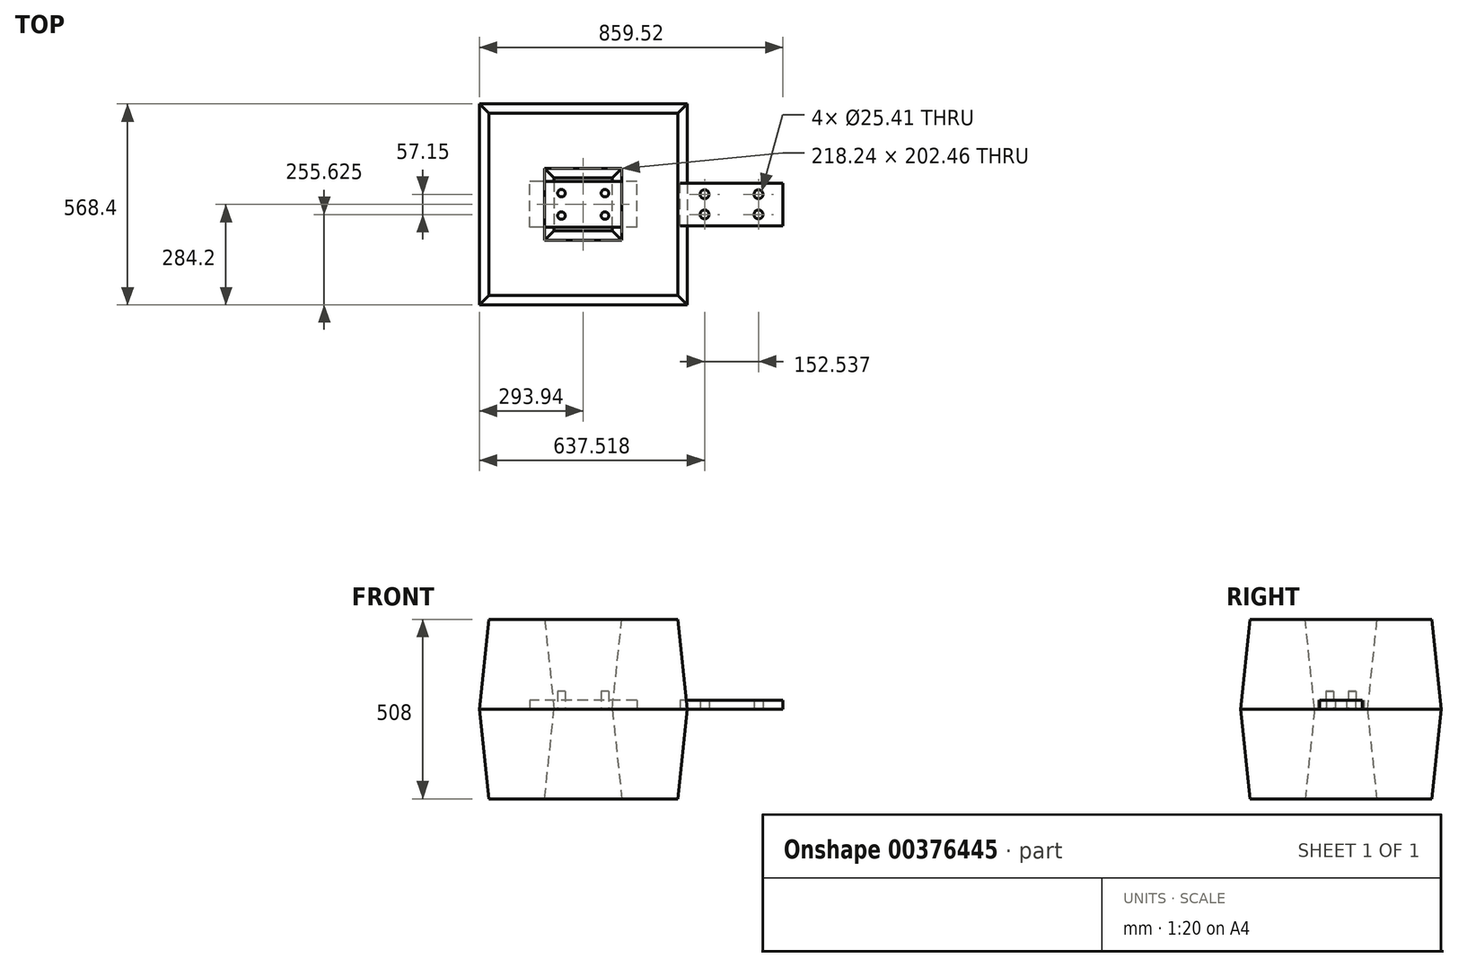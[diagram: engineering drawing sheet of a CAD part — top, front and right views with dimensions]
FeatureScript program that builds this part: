
annotation { "Feature Type Name" : "Feature", "Feature Type Description" : "" }
export const myFeature = defineFeature(function(context is Context, id is Id, definition is map)
    precondition{}
    {
        {
            var Q0;
            Q0=qCreatedBy(makeId("Top.planeOp"),FACE);
            var sketch = newSketch(context, id + "F0", { "sketchPlane" : qUnion([Q0])});
            skLineSegment(sketch, "E0.bottom", {"start": v(151.76, -65.22) * mm, "end": v(-151.76, -65.22) * mm});
            skLineSegment(sketch, "E0.top", {"start": v(151.76, 65.22) * mm, "end": v(-151.76, 65.22) * mm});
            skLineSegment(sketch, "E0.left", {"start": v(151.76, -65.22) * mm, "end": v(151.76, 65.22) * mm});
            skLineSegment(sketch, "E0.right", {"start": v(-151.76, -65.22) * mm, "end": v(-151.76, 65.22) * mm});
            skPoint(sketch, "E0.middle", {"position": v(0, 0) * mm});
            skSolve(sketch);
        }
        {
            var Q0;
            Q0 = qSketchRegion(id + "F0", true);
            extrude(context, id + "F1", {"entities" : qUnion([Q0]), "depth" : 25.4 * mm});
        }
        {
            var Q0;
            Q0=qCreatedBy(makeId("Top.planeOp"),FACE);
            var sketch = newSketch(context, id + "F2", { "sketchPlane" : qUnion([Q0])});
            skLineSegment(sketch, "E1.bottom", {"start": v(61.61, -31.77) * mm, "end": v(-61.61, -31.77) * mm, "construction": true});
            skLineSegment(sketch, "E1.top", {"start": v(61.61, 31.77) * mm, "end": v(-61.61, 31.77) * mm, "construction": true});
            skLineSegment(sketch, "E1.left", {"start": v(61.61, -31.77) * mm, "end": v(61.61, 31.77) * mm, "construction": true});
            skLineSegment(sketch, "E1.right", {"start": v(-61.61, -31.77) * mm, "end": v(-61.61, 31.77) * mm, "construction": true});
            skPoint(sketch, "E1.middle", {"position": v(0, 0) * mm});
            skCircle(sketch, "E2", {"center": v(61.61, -31.77) * mm, "radius": 10.6 * mm});
            skCircle(sketch, "E3", {"center": v(61.61, 31.77) * mm, "radius": 10.6 * mm});
            skCircle(sketch, "E4", {"center": v(-61.61, 31.77) * mm, "radius": 10.6 * mm});
            skCircle(sketch, "E5", {"center": v(-61.61, -31.77) * mm, "radius": 10.6 * mm});
            skSolve(sketch);
        }
        {
            var Q0;
            Q0 = qSketchRegion(id + "F2", true);
            extrude(context, id + "F3", {"entities" : qUnion([Q0]), "depth" : 50.8 * mm});
        }
        {
            var Q0;
            Q0=qCreatedBy(makeId("Top.planeOp"),FACE);
            var sketch = newSketch(context, id + "F4", { "sketchPlane" : qUnion([Q0])});
            skLineSegment(sketch, "E6.bottom", {"start": v(565.58, -60.24) * mm, "end": v(274.12, -60.24) * mm});
            skLineSegment(sketch, "E6.top", {"start": v(565.58, 60.24) * mm, "end": v(274.12, 60.24) * mm});
            skLineSegment(sketch, "E6.left", {"start": v(565.58, -60.24) * mm, "end": v(565.58, 60.24) * mm});
            skLineSegment(sketch, "E6.right", {"start": v(274.12, -60.24) * mm, "end": v(274.12, 60.24) * mm});
            skPoint(sketch, "E6.middle", {"position": v(419.85, 0) * mm});
            skLineSegment(sketch, "E7.bottom", {"start": v(496.11, -28.58) * mm, "end": v(343.58, -28.58) * mm, "construction": true});
            skLineSegment(sketch, "E7.top", {"start": v(496.11, 28.57) * mm, "end": v(343.58, 28.57) * mm, "construction": true});
            skLineSegment(sketch, "E7.left", {"start": v(496.11, -28.58) * mm, "end": v(496.11, 28.57) * mm, "construction": true});
            skLineSegment(sketch, "E7.right", {"start": v(343.58, -28.58) * mm, "end": v(343.58, 28.57) * mm, "construction": true});
            skCircle(sketch, "E8", {"center": v(343.58, 28.57) * mm, "radius": 12.7 * mm});
            skCircle(sketch, "E9", {"center": v(343.58, -28.58) * mm, "radius": 12.7 * mm});
            skCircle(sketch, "E10", {"center": v(496.11, -28.58) * mm, "radius": 12.7 * mm});
            skCircle(sketch, "E11", {"center": v(496.11, 28.57) * mm, "radius": 12.7 * mm});
            skSolve(sketch);
        }
        {
            var Q0;
            Q0 = qSketchRegion(id + "F4", true);
            extrude(context, id + "F5", {"entities" : qUnion([Q0]), "depth" : 25.4 * mm});
        }
        {
            var Q0;
            Q0=qCreatedBy(makeId("Top.planeOp"),FACE);
            var sketch = newSketch(context, id + "F6", { "sketchPlane" : qUnion([Q0])});
            skLineSegment(sketch, "E12.bottom", {"start": v(293.94, -284.2) * mm, "end": v(-293.94, -284.2) * mm});
            skLineSegment(sketch, "E12.top", {"start": v(293.94, 284.2) * mm, "end": v(-293.94, 284.2) * mm});
            skLineSegment(sketch, "E12.left", {"start": v(293.94, -284.2) * mm, "end": v(293.94, 284.2) * mm});
            skLineSegment(sketch, "E12.right", {"start": v(-293.94, -284.2) * mm, "end": v(-293.94, 284.2) * mm});
            skPoint(sketch, "E12.middle", {"position": v(0, 0) * mm});
            skLineSegment(sketch, "E13.bottom", {"start": v(82.42, -74.53) * mm, "end": v(-82.42, -74.53) * mm});
            skLineSegment(sketch, "E13.top", {"start": v(82.42, 74.53) * mm, "end": v(-82.42, 74.53) * mm});
            skLineSegment(sketch, "E13.left", {"start": v(82.42, -74.53) * mm, "end": v(82.42, 74.53) * mm});
            skLineSegment(sketch, "E13.right", {"start": v(-82.42, -74.53) * mm, "end": v(-82.42, 74.53) * mm});
            skSolve(sketch);
        }
        {
            var Q0;
            Q0 = qSketchRegion(id + "F6", true);
            extrude(context, id + "F7", {"entities" : qUnion([Q0]), "endBound" : BoundingType.SYMMETRIC, "depth" : 508 * mm, "hasDraft" : true, "draftAngle" : 6 * degree, "draftPullDirection" : true});
        }
    });
